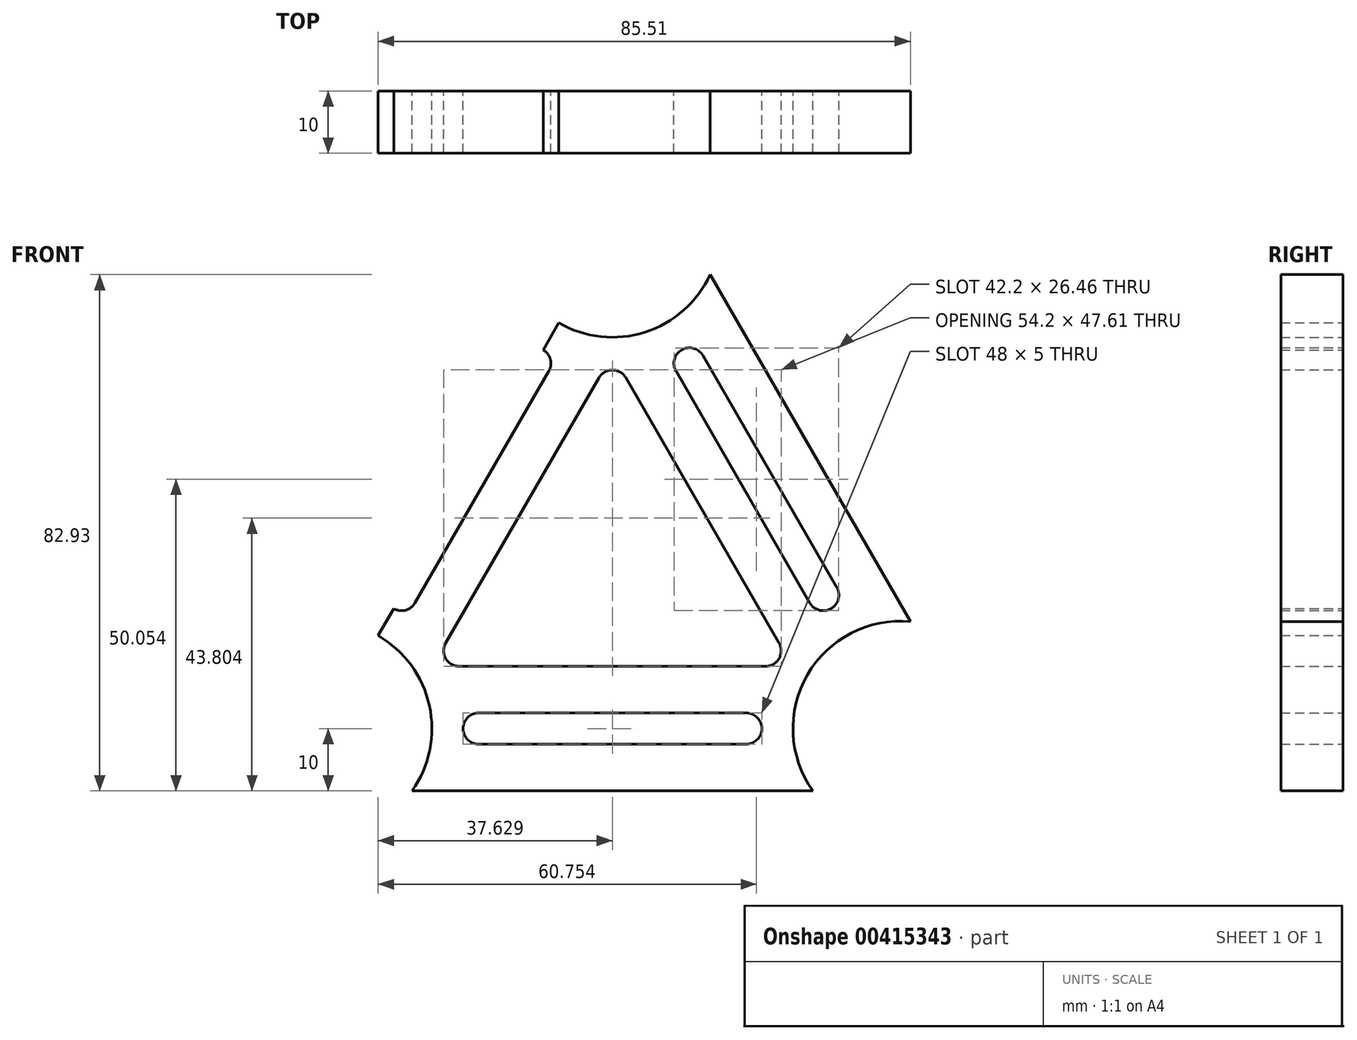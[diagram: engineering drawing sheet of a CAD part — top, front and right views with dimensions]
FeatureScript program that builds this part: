
annotation { "Feature Type Name" : "Feature", "Feature Type Description" : "" }
export const myFeature = defineFeature(function(context is Context, id is Id, definition is map)
    precondition{}
    {
        {
            var Q0;
            Q0=qCreatedBy(makeId("Front.planeOp"),FACE);
            var sketch = newSketch(context, id + "F0", { "sketchPlane" : qUnion([Q0])});
            skPoint(sketch, "E0", {"position": v(-53.68, 0) * mm});
            skArc(sketch, "E1", {"start": v(-39.63, -10) * mm, "mid": v(-38.74, 8.62) * mm, "end": v(-55.31, 17.17) * mm});
            skArc(sketch, "E2", {"start": v(40.45, 17.17) * mm, "mid": v(23.88, 8.62) * mm, "end": v(24.76, -10) * mm});
            skLineSegment(sketch, "E3", {"start": v(-36.43, 0) * mm, "end": v(21.57, 0) * mm});
            skLineSegment(sketch, "E4", {"start": v(30.2, 14.94) * mm, "end": v(5.29, 58.08) * mm});
            skLineSegment(sketch, "E5", {"start": v(30.2, 14.94) * mm, "end": v(1.2, 65.17) * mm});
            skPoint(sketch, "E5.endSnap0", {"position": v(-7.43, 0) * mm});
            skLineSegment(sketch, "E6", {"start": v(-16.06, 65.17) * mm, "end": v(-45.06, 14.94) * mm});
            skArc(sketch, "E7", {"start": v(-23.12, 72.93) * mm, "mid": v(-7.43, 62.86) * mm, "end": v(8.26, 72.93) * mm});
            skPoint(sketch, "E8", {"position": v(-45.06, 14.94) * mm});
            skPoint(sketch, "E9", {"position": v(-16.06, 65.17) * mm});
            skPoint(sketch, "E10", {"position": v(1.2, 65.17) * mm});
            skPoint(sketch, "E11", {"position": v(30.2, 14.94) * mm});
            skPoint(sketch, "E12", {"position": v(21.57, 0) * mm});
            skPoint(sketch, "E13", {"position": v(-36.43, 0) * mm});
            skLineSegment(sketch, "E14", {"start": v(-24.72, 70.17) * mm, "end": v(-53.72, 19.94) * mm});
            skLineSegment(sketch, "E15", {"start": v(-53.72, 19.94) * mm, "end": v(-55.31, 17.17) * mm});
            skLineSegment(sketch, "E16", {"start": v(-24.72, 70.17) * mm, "end": v(-23.12, 72.93) * mm});
            skLineSegment(sketch, "E17.0", {"start": v(-23.12, 72.93) * mm, "end": v(-55.31, 17.17) * mm});
            skLineSegment(sketch, "E17.1", {"start": v(40.45, 17.17) * mm, "end": v(8.26, 72.93) * mm});
            skLineSegment(sketch, "E17.2", {"start": v(-39.63, -10) * mm, "end": v(24.76, -10) * mm});
            skPoint(sketch, "E18", {"position": v(-28.93, 0) * mm});
            skPoint(sketch, "E19", {"position": v(14.07, 0) * mm});
            skCircle(sketch, "E20", {"center": v(14.07, 0) * mm, "radius": 2.5 * mm});
            skCircle(sketch, "E21", {"center": v(-28.93, 0) * mm, "radius": 2.5 * mm});
            skLineSegment(sketch, "E22", {"start": v(-28.93, 2.5) * mm, "end": v(14.07, 2.5) * mm});
            skLineSegment(sketch, "E23", {"start": v(14.07, -2.5) * mm, "end": v(-28.93, -2.5) * mm});
            skPoint(sketch, "E24", {"position": v(26.44, 21.43) * mm});
            skPoint(sketch, "E25", {"position": v(4.94, 58.67) * mm});
            skCircle(sketch, "E26", {"center": v(4.94, 58.67) * mm, "radius": 2.5 * mm});
            skCircle(sketch, "E27", {"center": v(26.44, 21.43) * mm, "radius": 2.5 * mm});
            skPoint(sketch, "E28", {"position": v(10.13, 49.7) * mm});
            skLineSegment(sketch, "E29", {"start": v(10.13, 49.7) * mm, "end": v(12.3, 50.94) * mm});
            skLineSegment(sketch, "E30", {"start": v(4.94, 58.67) * mm, "end": v(7.1, 59.92) * mm});
            skLineSegment(sketch, "E31", {"start": v(26.44, 21.43) * mm, "end": v(28.6, 22.68) * mm});
            skLineSegment(sketch, "E32", {"start": v(28.6, 22.68) * mm, "end": v(7.1, 59.92) * mm});
            skLineSegment(sketch, "E33", {"start": v(4.94, 58.67) * mm, "end": v(2.78, 57.42) * mm});
            skLineSegment(sketch, "E34", {"start": v(26.44, 21.43) * mm, "end": v(24.28, 20.18) * mm});
            skLineSegment(sketch, "E35", {"start": v(24.28, 20.18) * mm, "end": v(2.78, 57.42) * mm});
            skPoint(sketch, "E36", {"position": v(-41.3, 21.43) * mm});
            skCircle(sketch, "E37", {"center": v(-41.3, 21.43) * mm, "radius": 2.5 * mm});
            skCircle(sketch, "E38", {"center": v(-19.8, 58.67) * mm, "radius": 2.5 * mm});
            skLineSegment(sketch, "E39", {"start": v(-19.8, 58.67) * mm, "end": v(-17.64, 57.42) * mm});
            skLineSegment(sketch, "E40", {"start": v(-17.64, 57.42) * mm, "end": v(-19.8, 58.67) * mm});
            skLineSegment(sketch, "E41", {"start": v(-19.8, 58.67) * mm, "end": v(-21.97, 59.92) * mm});
            skLineSegment(sketch, "E42", {"start": v(-41.3, 21.43) * mm, "end": v(-39.14, 20.18) * mm});
            skLineSegment(sketch, "E43", {"start": v(-39.14, 20.18) * mm, "end": v(-41.3, 21.43) * mm});
            skLineSegment(sketch, "E44", {"start": v(-41.3, 21.43) * mm, "end": v(-43.47, 22.68) * mm});
            skLineSegment(sketch, "E45", {"start": v(-39.14, 20.18) * mm, "end": v(-17.64, 57.42) * mm});
            skLineSegment(sketch, "E46", {"start": v(-43.47, 22.68) * mm, "end": v(-21.97, 59.92) * mm});
            skPoint(sketch, "E47", {"position": v(-7.43, 55.36) * mm});
            skPoint(sketch, "E47.positionSnap0", {"position": v(-7.43, 62.86) * mm});
            skLineSegment(sketch, "E48", {"start": v(-7.43, 80.1) * mm, "end": v(-53.68, 0) * mm, "construction": true});
            skLineSegment(sketch, "E49", {"start": v(-7.43, 80.1) * mm, "end": v(38.82, 0) * mm, "construction": true});
            skLineSegment(sketch, "E50", {"start": v(38.82, 0) * mm, "end": v(-53.68, 0) * mm, "construction": true});
            skLineSegment(sketch, "E51.0", {"start": v(-9.6, 56.36) * mm, "end": v(-34.2, 13.75) * mm});
            skLineSegment(sketch, "E51.1", {"start": v(-5.27, 56.36) * mm, "end": v(19.33, 13.75) * mm});
            skLineSegment(sketch, "E51.2", {"start": v(17.17, 10) * mm, "end": v(-32.03, 10) * mm});
            skPoint(sketch, "E52.visualSharp", {"position": v(-7.43, 60.1) * mm});
            skArc(sketch, "E52.filletArc", {"start": v(-5.27, 56.36) * mm, "mid": v(-7.43, 57.6) * mm, "end": v(-9.6, 56.36) * mm});
            skPoint(sketch, "E53.visualSharp", {"position": v(-36.36, 10) * mm});
            skArc(sketch, "E53.filletArc", {"start": v(-34.2, 13.75) * mm, "mid": v(-34.2, 11.25) * mm, "end": v(-32.03, 10) * mm});
            skPoint(sketch, "E54.visualSharp", {"position": v(21.5, 10) * mm});
            skArc(sketch, "E54.filletArc", {"start": v(17.17, 10) * mm, "mid": v(19.33, 11.25) * mm, "end": v(19.33, 13.75) * mm});
            skSolve(sketch);
        }
        {
            var Q0;
            {var subQ9=sQuery(id+"F0.wireOp",EDGE,"E17.0");Q0=makeQuery(id+"F0.imprint","IMPRINT",FACE,{"disambiguationData":[TD([[makeQuery(id+"F0.imprint","IMPRINT",EDGE,{"derivedFrom":subQ9}),1.0]])]});}
            var Q1;
            {var subQ9=sQuery(id+"F0.wireOp",EDGE,"E22");Q1=makeQuery(id+"F0.imprint","IMPRINT",FACE,{"disambiguationData":[TD([[makeQuery(id+"F0.imprint","IMPRINT",EDGE,{"derivedFrom":subQ9}),1.0]])]});}
            var Q2;
            {var subQ3=sQuery(id+"F0.wireOp",EDGE,"E17.1");Q2=makeQuery(id+"F0.imprint","IMPRINT",FACE,{"disambiguationData":[TD([[makeQuery(id+"F0.imprint","IMPRINT",EDGE,{"derivedFrom":subQ3}),1.0]])]});}
            var Q3;
            {var subQ10=sQuery(id+"F0.wireOp",EDGE,"E17.2");Q3=makeQuery(id+"F0.imprint","IMPRINT",FACE,{"disambiguationData":[TD([[makeQuery(id+"F0.imprint","IMPRINT",EDGE,{"derivedFrom":subQ10}),1.0]])]});}
            extrude(context, id + "F1", {"entities" : qUnion([Q0, Q1, Q2, Q3]), "depth" : 10 * mm});
        }
    });
